# Revit family: Haworth_BuzziBracks_Shelf_Side_BUILD
name_source: partatom
category: Furniture
revit_build: Autodesk Revit 2018 (Build: 20170223_1515(x64)
units: mm (PartAtom-declared; Revit-internal decimal feet)

## family parameters
Always vertical = Yes
Cut with Voids When Loaded = No
OmniClass Number = 23.40.20.00
OmniClass Title = General Furniture and Specialties
Room Calculation Point = No
Shared = No
Work Plane-Based = No

## types (1)
- BRS - Side Shelf
    Actual Depth = 11.5 "
    Actual Height = 29.75 "
    Actual Width = 31.25 "
    Assembly Code = E2020200
    Description = Haworth - BuzziBracks - Side Shelf
    Manufacturer = Haworth
    Model = HCBZ-BRW
    Note = Verify Final Dim. w/ Haworth
    Revision = 1
    Thickness = 1.75 "
    Top Radius = 4 "
    URL = http://www.haworth.com
    URL - Product = http://www.haworth.com
    Warranty = http://www.haworth.com

## geometry (parser evidence)
native form markers: Sweep x2
no freeform markers — native parametric forms only
